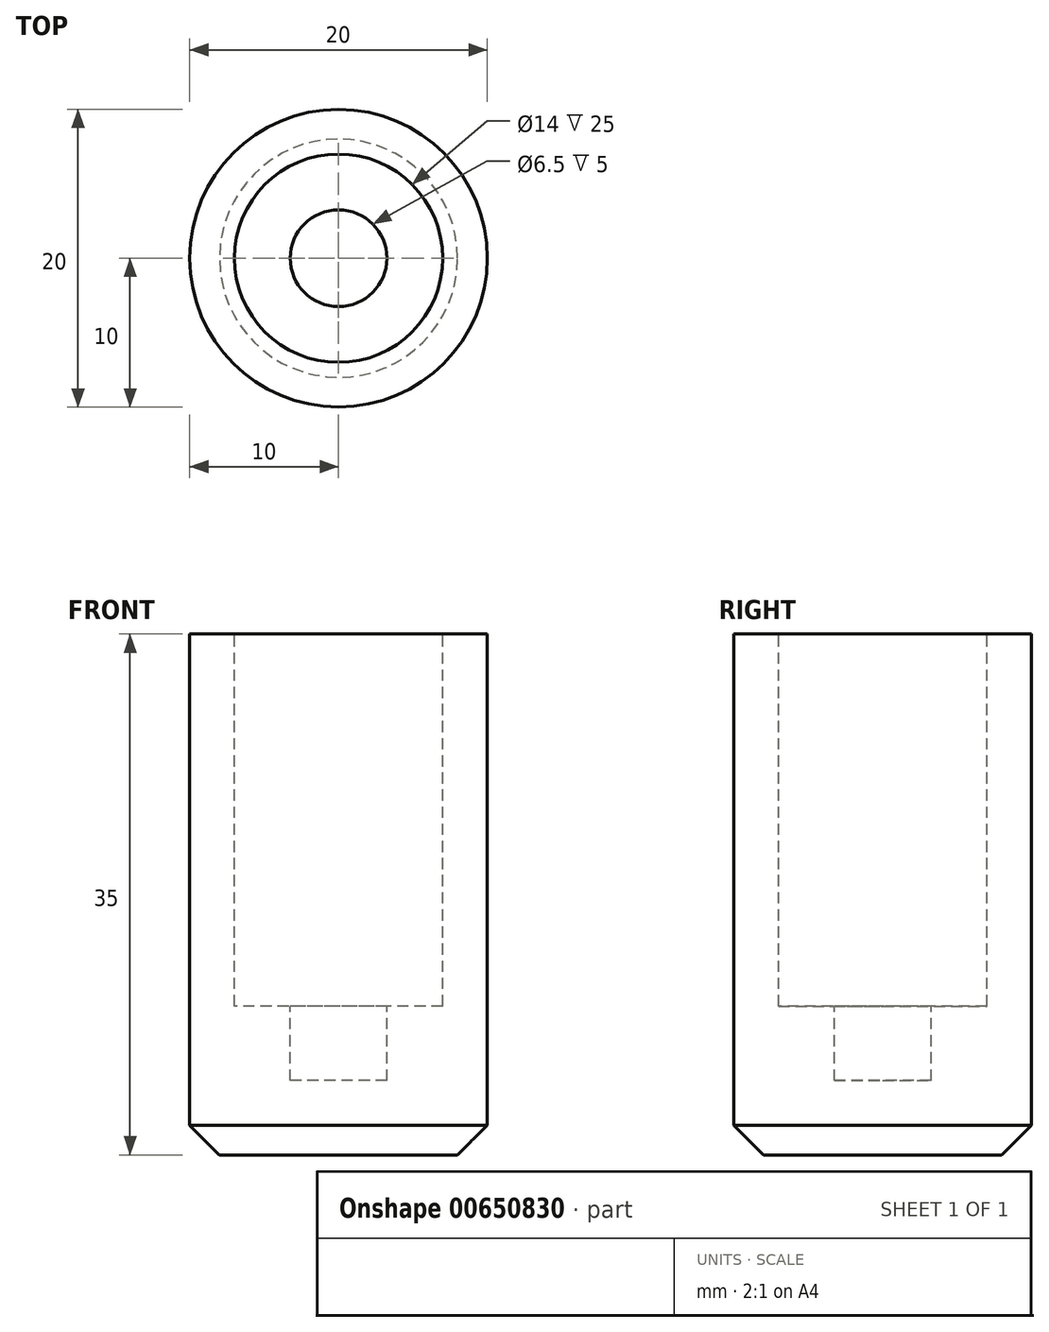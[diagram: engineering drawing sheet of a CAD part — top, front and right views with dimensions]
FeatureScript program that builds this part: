
annotation { "Feature Type Name" : "Feature", "Feature Type Description" : "" }
export const myFeature = defineFeature(function(context is Context, id is Id, definition is map)
    precondition{}
    {
        {
            var Q0;
            Q0=qCreatedBy(makeId("Top.planeOp"),FACE);
            var sketch = newSketch(context, id + "F0", { "sketchPlane" : qUnion([Q0])});
            skCircle(sketch, "E0", {"center": v(0, 0) * mm, "radius": 10 * mm});
            skSolve(sketch);
        }
        {
            var Q0;
            Q0=makeQuery(id+"F0.imprint","IMPRINT",FACE,{"disambiguationData":[TD([[makeQuery(id+"F0.imprint","IMPRINT",EDGE,{"derivedFrom":sQuery(id+"F0.wireOp",EDGE,"E0")}),1.0]])]});
            extrude(context, id + "F1", {"entities" : qUnion([Q0]), "depth" : 35 * mm, "offsetDistance" : 25 * mm});
        }
        {
            var Q0;
            Q0=makeQuery(id+"F1.opExtrude","CAP_FACE",FACE,{"disambiguationData":[OSD([sQuery(id+"F0.wireOp",EDGE,"E0")])],"isStart":false});
            var sketch = newSketch(context, id + "F2", { "sketchPlane" : qUnion([Q0])});
            skCircle(sketch, "E1", {"center": v(0, 0) * mm, "radius": 7 * mm});
            skSolve(sketch);
        }
        {
            var Q0;
            Q0=makeQuery(id+"F1.opExtrude","CAP_FACE",FACE,{"disambiguationData":[OSD([sQuery(id+"F0.wireOp",EDGE,"E0")])],"isStart":false});
            var sketch = newSketch(context, id + "F3", { "sketchPlane" : qUnion([Q0])});
            skCircle(sketch, "E2", {"center": v(0, 0) * mm, "radius": 3.25 * mm});
            skSolve(sketch);
        }
        {
            var Q0;
            Q0 = qSketchRegion(id + "F2", true);
            extrude(context, id + "F4", {"entities" : qUnion([Q0]), "operationType" : NewBodyOperationType.REMOVE, "oppositeDirection" : true, "depth" : 25 * mm, "offsetDistance" : 25 * mm});
        }
        {
            var Q0;
            Q0 = qSketchRegion(id + "F3", true);
            extrude(context, id + "F5", {"entities" : qUnion([Q0]), "operationType" : NewBodyOperationType.REMOVE, "oppositeDirection" : true, "depth" : 30 * mm, "offsetDistance" : 25 * mm});
        }
        {
            var Q0;
            Q0=makeQuery(id+"F1.opExtrude","CAP_EDGE",EDGE,{"disambiguationData":[OSD([sQuery(id+"F0.wireOp",EDGE,"E0")])],"isStart":true});
            chamfer(context, id + "F6", {"entities" : qUnion([Q0]), "width" : 2 * mm, "tangentPropagation" : true});
        }
    });
